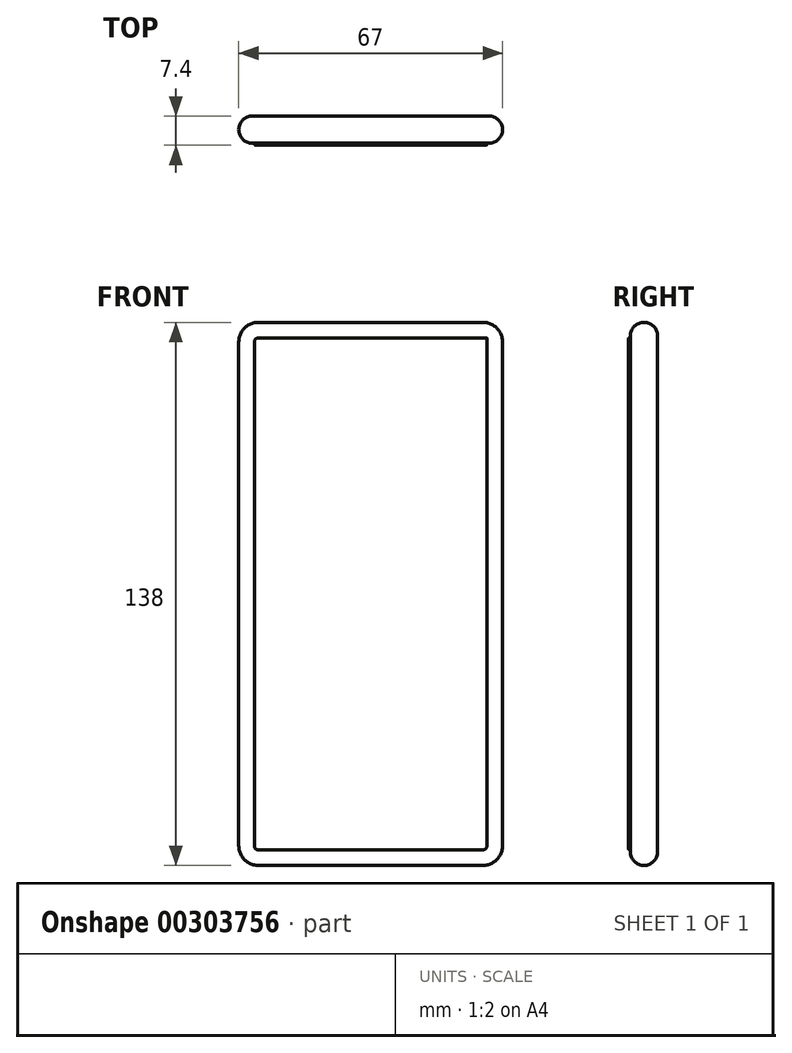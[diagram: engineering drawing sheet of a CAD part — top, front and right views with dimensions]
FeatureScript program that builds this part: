
annotation { "Feature Type Name" : "Feature", "Feature Type Description" : "" }
export const myFeature = defineFeature(function(context is Context, id is Id, definition is map)
    precondition{}
    {
        {
            var Q0;
            Q0=qCreatedBy(makeId("Front.planeOp"),FACE);
            var sketch = newSketch(context, id + "F0", { "sketchPlane" : qUnion([Q0])});
            skLineSegment(sketch, "E0.bottom", {"start": v(0, 0) * mm, "end": v(67, 0) * mm});
            skLineSegment(sketch, "E0.top", {"start": v(0, 138) * mm, "end": v(67, 138) * mm});
            skLineSegment(sketch, "E0.left", {"start": v(0, 0) * mm, "end": v(0, 138) * mm});
            skLineSegment(sketch, "E0.right", {"start": v(67, 0) * mm, "end": v(67, 138) * mm});
            skSolve(sketch);
        }
        {
            var Q0;
            Q0=makeQuery(id+"F0.imprint","IMPRINT",FACE,{"disambiguationData":[TD([[makeQuery(id+"F0.imprint","IMPRINT",EDGE,{"derivedFrom":sQuery(id+"F0.wireOp",EDGE,"E0.bottom")}),1.0]])]});
            extrude(context, id + "F1", {"entities" : qUnion([Q0]), "oppositeDirection" : true, "depth" : 6.9 * mm});
        }
        {
            var Q0;
            Q0=makeQuery(id+"F1.opExtrude","SWEPT_EDGE",EDGE,{"disambiguationData":[OSD([sQuery(id+"F0.wireOp",EDGE,"E0.top"),sQuery(id+"F0.wireOp",EDGE,"E0.right")])]});
            var Q1;
            Q1=makeQuery(id+"F1.opExtrude","SWEPT_EDGE",EDGE,{"disambiguationData":[OSD([sQuery(id+"F0.wireOp",EDGE,"E0.bottom"),sQuery(id+"F0.wireOp",EDGE,"E0.right")])]});
            var Q2;
            Q2=makeQuery(id+"F1.opExtrude","SWEPT_EDGE",EDGE,{"disambiguationData":[OSD([sQuery(id+"F0.wireOp",EDGE,"E0.top"),sQuery(id+"F0.wireOp",EDGE,"E0.left")])]});
            var Q3;
            Q3=makeQuery(id+"F1.opExtrude","SWEPT_EDGE",EDGE,{"disambiguationData":[OSD([sQuery(id+"F0.wireOp",EDGE,"E0.bottom"),sQuery(id+"F0.wireOp",EDGE,"E0.left")])]});
            fillet(context, id + "F2", {"entities" : qUnion([Q0, Q1, Q2, Q3]), "radius" : 5 * mm, "tangentPropagation" : true, "allowEdgeOverflow" : false});
        }
        {
            var Q0;
            Q0=makeQuery(id+"F1.opExtrude","CAP_EDGE",EDGE,{"disambiguationData":[OSD([sQuery(id+"F0.wireOp",EDGE,"E0.right")])],"isStart":true});
            var Q1;
            Q1=makeQuery(id+"F1.opExtrude","CAP_FACE",FACE,{"disambiguationData":[OSD([sQuery(id+"F0.wireOp",EDGE,"E0.bottom"),sQuery(id+"F0.wireOp",EDGE,"E0.top"),sQuery(id+"F0.wireOp",EDGE,"E0.left"),sQuery(id+"F0.wireOp",EDGE,"E0.right")])],"isStart":false});
            fillet(context, id + "F3", {"entities" : qUnion([Q0, Q1]), "radius" : 6.9 / 2 * mm, "tangentPropagation" : true, "allowEdgeOverflow" : false});
        }
        {
            var Q0;
            Q0=makeQuery(id+"F1.opExtrude","CAP_FACE",FACE,{"disambiguationData":[OSD([sQuery(id+"F0.wireOp",EDGE,"E0.bottom"),sQuery(id+"F0.wireOp",EDGE,"E0.top"),sQuery(id+"F0.wireOp",EDGE,"E0.left"),sQuery(id+"F0.wireOp",EDGE,"E0.right")])],"isStart":true});
            var sketch = newSketch(context, id + "F4", { "sketchPlane" : qUnion([Q0])});
            skSolve(sketch);
        }
        {
            var Q0;
            {var subQ0=sQuery(id+"F0.wireOp",EDGE,"E0.right");var subQ1=sQuery(id+"F0.wireOp",EDGE,"E0.left");var subQ2=sQuery(id+"F0.wireOp",EDGE,"E0.top");var subQ3=sQuery(id+"F0.wireOp",EDGE,"E0.bottom");var subQ4=makeQuery(id+"F1.opExtrude","CAP_FACE",FACE,{"disambiguationData":[OSD([subQ3,subQ2,subQ1,subQ0])],"isStart":true});var subQ5=subQ4;Q0=makeQuery(id+"F4.imprint","IMPRINT",FACE,{"disambiguationData":[TD([[makeQuery(id+"F4.imprint","IMPRINT",EDGE,{"derivedFrom":makeQuery(id+"F3.opFillet","BLEND_EDGE",EDGE,{"blendedFrom":[makeQuery(id+"F1.opExtrude","CAP_EDGE",EDGE,{"disambiguationData":[OSD([subQ3])],"isStart":true}),subQ5],"blendedInto":[subQ5]})}),1.0]])]});}
            var sketch = newSketch(context, id + "F5", { "sketchPlane" : qUnion([Q0])});
            skLineSegment(sketch, "E1.0", {"start": v(3.95, 133) * mm, "end": v(3.95, 5) * mm});
            skArc(sketch, "E1.1", {"start": v(5, 134.05) * mm, "mid": v(4.26, 133.74) * mm, "end": v(3.95, 133) * mm});
            skArc(sketch, "E2.0", {"start": v(3.95, 5) * mm, "mid": v(4.26, 4.26) * mm, "end": v(5, 3.95) * mm});
            skLineSegment(sketch, "E3.0", {"start": v(5, 3.95) * mm, "end": v(62, 3.95) * mm});
            skLineSegment(sketch, "E4.0", {"start": v(63.05, 134.05) * mm, "end": v(5, 134.05) * mm});
            skLineSegment(sketch, "E4.1", {"start": v(63.05, 5) * mm, "end": v(63.05, 134.05) * mm});
            skArc(sketch, "E5.0", {"start": v(62, 3.95) * mm, "mid": v(62.74, 4.26) * mm, "end": v(63.05, 5) * mm});
            skSolve(sketch);
        }
        {
            var Q0;
            Q0=qSketchRegion(id+"F5",true);
            extrude(context, id + "F6", {"entities" : qUnion([Q0]), "operationType" : NewBodyOperationType.ADD, "depth" : .5 * mm});
        }
        {
            var Q0;
            Q0=makeQuery(id+"F6.opExtrude","CAP_EDGE",EDGE,{"disambiguationData":[OSD([sQuery(id+"F5.wireOp",EDGE,"E1.0")])],"isStart":false});
            fillet(context, id + "F7", {"entities" : qUnion([Q0]), "radius" : .25 * mm, "tangentPropagation" : true, "allowEdgeOverflow" : false});
        }
    });
